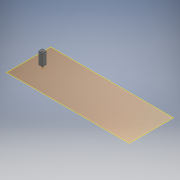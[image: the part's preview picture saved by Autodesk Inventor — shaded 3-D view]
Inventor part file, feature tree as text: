
AUTODESK INVENTOR PART (.ipt)
format: ipt  version: 2017 (Build 210142000, 142)  size: 125,952 bytes
history: native  units: mm
features: other x3, plane x2, extrude x2, sketch x2, reference x2, chamfer x1
ambient origin geometry x8: Origin, YZ Plane, XZ Plane, XY Plane, X Axis, Y Axis, Z Axis, Center Point
bodies: Solid1 (feature_tree), Solid2 (feature_tree)
feature tree (12):
  plane  "Work Plane1"
  extrude  "Extrusion1"  Depth=0.5mm
  plane  "Work Plane2"
  extrude  "Extrusion2"  Depth=2.54mm
  chamfer  "Chamfer1"  Distance=2.54mm
  sketch  "Sketch1"  dims[d0=0.5mm d1=0.5mm]
  reference  "Reference1"
  sketch  "Sketch2"  dims[d2=2.0mm d3=0.0mm d4=2.54mm d5=2.54mm d6=8.0mm d7=0.0mm d8=0.5mm d9=2.0mm d10=45.0deg]
  reference  "Reference2"
  parser-record x1  (decoder bookkeeping rows leaked as tree rows — omitted from the tree; the rows remain in map.json)
  other  "protoswitchboard.iam"
  other  "Board:1"
note: 1 file-system path scrubbed to <path> (originals preserved in map.json)
